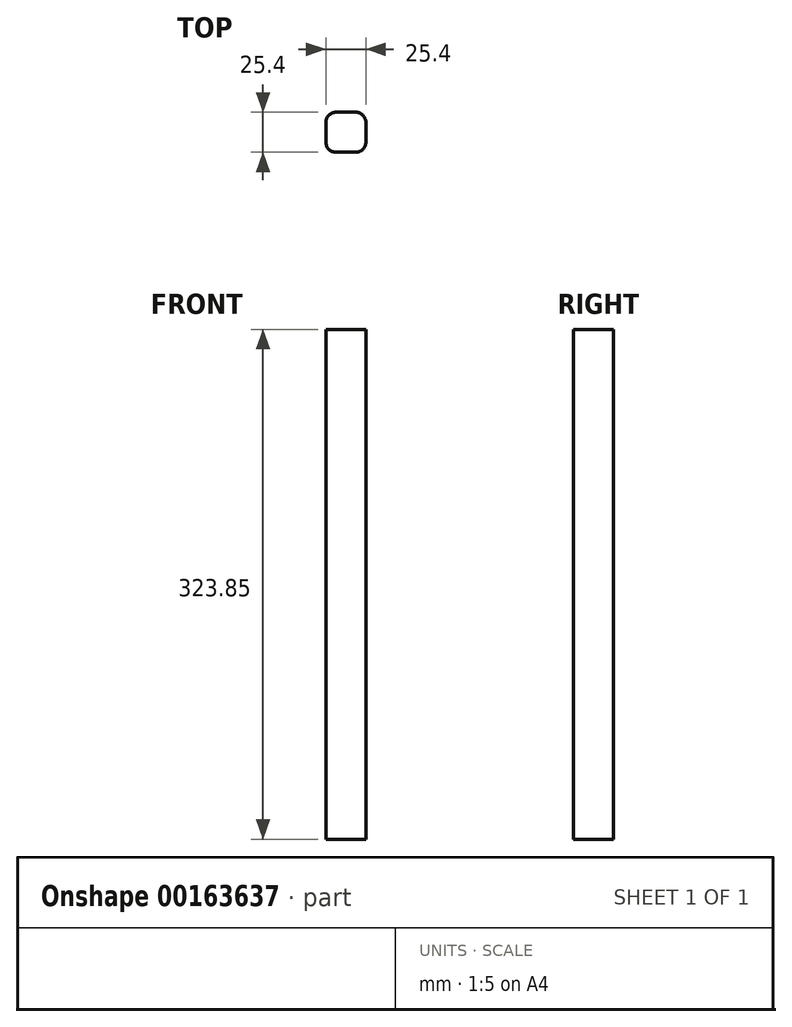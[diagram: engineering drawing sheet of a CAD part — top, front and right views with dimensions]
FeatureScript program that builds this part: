
annotation { "Feature Type Name" : "Feature", "Feature Type Description" : "" }
export const myFeature = defineFeature(function(context is Context, id is Id, definition is map)
    precondition{}
    {
        {
            var Q0;
            Q0=qCreatedBy(makeId("Top.planeOp"),FACE);
            var sketch = newSketch(context, id + "F0", { "sketchPlane" : qUnion([Q0])});
            skLineSegment(sketch, "E0.bottom", {"start": v(6.35, 12.7) * mm, "end": v(-6.35, 12.7) * mm});
            skLineSegment(sketch, "E0.top", {"start": v(6.35, -12.7) * mm, "end": v(-6.35, -12.7) * mm});
            skLineSegment(sketch, "E0.left", {"start": v(12.7, 6.35) * mm, "end": v(12.7, -6.35) * mm});
            skLineSegment(sketch, "E0.right", {"start": v(-12.7, 6.35) * mm, "end": v(-12.7, -6.35) * mm});
            skPoint(sketch, "E0.middle", {"position": v(0, 0) * mm});
            skPoint(sketch, "E1.visualSharp", {"position": v(-12.7, 12.7) * mm});
            skArc(sketch, "E1.filletArc", {"start": v(-6.35, 12.7) * mm, "mid": v(-10.84, 10.84) * mm, "end": v(-12.7, 6.35) * mm});
            skPoint(sketch, "E2.visualSharp", {"position": v(-12.7, -12.7) * mm});
            skArc(sketch, "E2.filletArc", {"start": v(-12.7, -6.35) * mm, "mid": v(-10.84, -10.84) * mm, "end": v(-6.35, -12.7) * mm});
            skPoint(sketch, "E3.visualSharp", {"position": v(12.7, -12.7) * mm});
            skArc(sketch, "E3.filletArc", {"start": v(6.35, -12.7) * mm, "mid": v(10.84, -10.84) * mm, "end": v(12.7, -6.35) * mm});
            skPoint(sketch, "E4.visualSharp", {"position": v(12.7, 12.7) * mm});
            skArc(sketch, "E4.filletArc", {"start": v(12.7, 6.35) * mm, "mid": v(10.84, 10.84) * mm, "end": v(6.35, 12.7) * mm});
            skSolve(sketch);
        }
        {
            var Q0;
            Q0=qSketchRegion(id+"F0",true);
            extrude(context, id + "F1", {"entities" : qUnion([Q0]), "depth" : 323.85 * mm, "offsetDistance" : 25.4 * mm});
        }
    });
